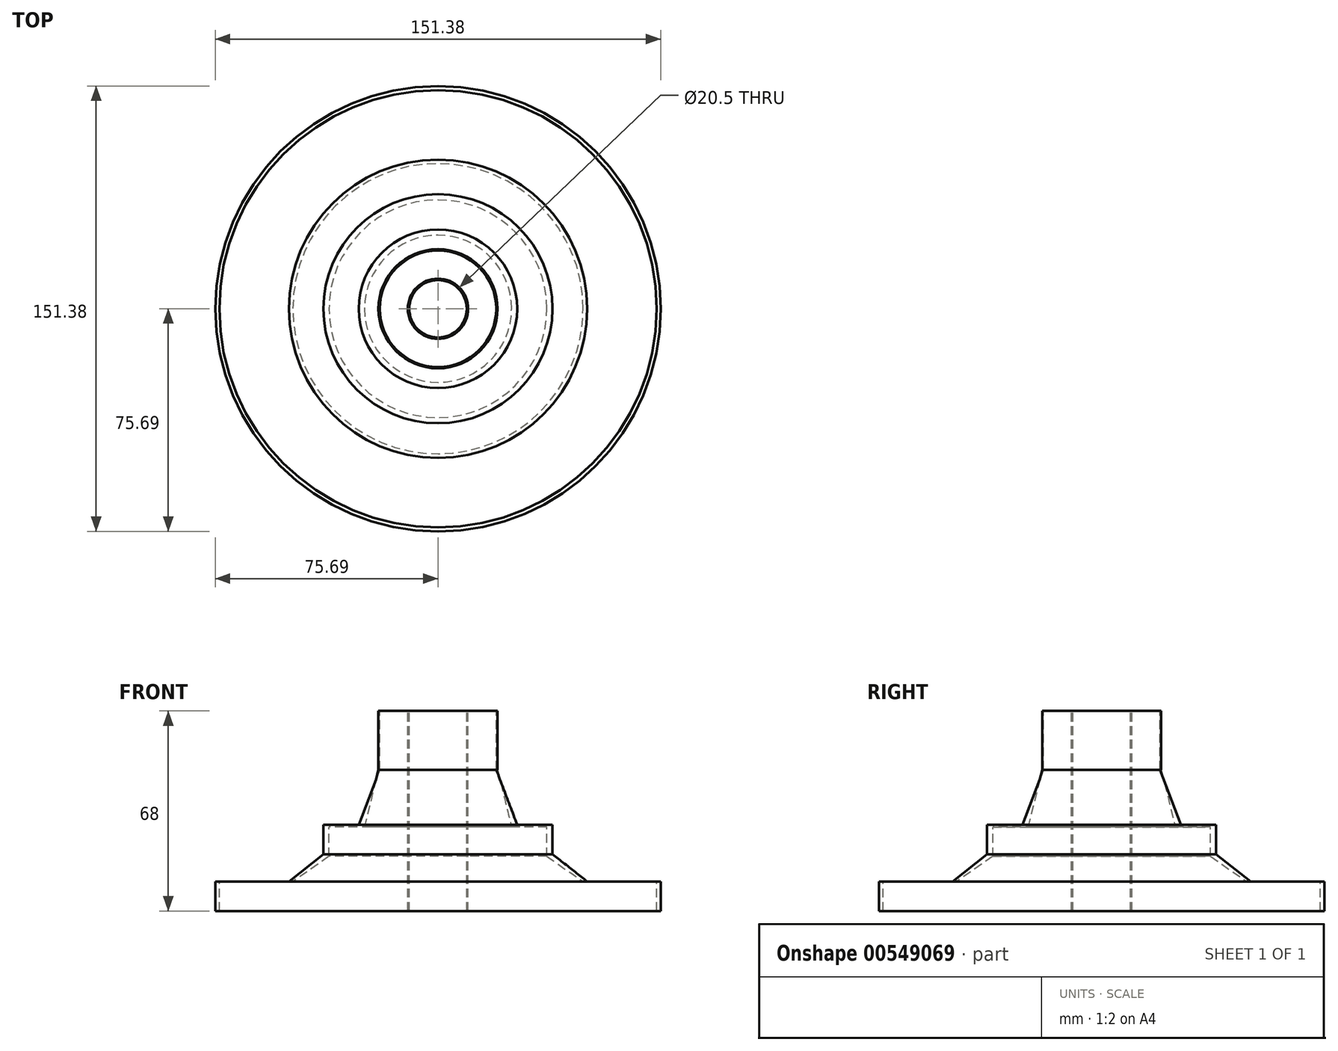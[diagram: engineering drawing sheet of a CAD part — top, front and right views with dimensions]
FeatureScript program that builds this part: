
annotation { "Feature Type Name" : "Feature", "Feature Type Description" : "" }
export const myFeature = defineFeature(function(context is Context, id is Id, definition is map)
    precondition{}
    {
        {
            var Q0;
            Q0=qCreatedBy(makeId("Front.planeOp"),FACE);
            var sketch = newSketch(context, id + "F0", { "sketchPlane" : qUnion([Q0])});
            skLineSegment(sketch, "E0", {"start": v(0, 68) * mm, "end": v(10, 68) * mm, "construction": true});
            skLineSegment(sketch, "E1", {"start": v(10, 68) * mm, "end": v(-10, 68) * mm, "construction": true});
            skLineSegment(sketch, "E2", {"start": v(-10, 68) * mm, "end": v(-10, 0) * mm, "construction": true});
            skLineSegment(sketch, "E3", {"start": v(-10, 0) * mm, "end": v(10, 0) * mm, "construction": true});
            skLineSegment(sketch, "E4", {"start": v(10, 0) * mm, "end": v(10, 68) * mm, "construction": true});
            skLineSegment(sketch, "E5", {"start": v(10, 68) * mm, "end": v(20, 68) * mm, "construction": true});
            skLineSegment(sketch, "E6", {"start": v(20, 68) * mm, "end": v(-20, 68) * mm, "construction": true});
            skLineSegment(sketch, "E7", {"start": v(-20, 68) * mm, "end": v(-20, 48) * mm, "construction": true});
            skLineSegment(sketch, "E8", {"start": v(20, 68) * mm, "end": v(20, 48) * mm, "construction": true});
            skLineSegment(sketch, "E9", {"start": v(0, 68) * mm, "end": v(0, 27.84) * mm, "construction": true});
            skLineSegment(sketch, "E10", {"start": v(0, 27.84) * mm, "end": v(-37.5, 27.84) * mm, "construction": true});
            skLineSegment(sketch, "E11", {"start": v(0, 27.84) * mm, "end": v(37.5, 27.84) * mm, "construction": true});
            skLineSegment(sketch, "E12", {"start": v(0, 68) * mm, "end": v(0, 18) * mm, "construction": true});
            skLineSegment(sketch, "E13", {"start": v(0, 68) * mm, "end": v(0, 10) * mm, "construction": true});
            skPoint(sketch, "E13.endSnap0", {"position": v(0, 43) * mm});
            skLineSegment(sketch, "E14", {"start": v(0, 10) * mm, "end": v(50, 10) * mm, "construction": true});
            skLineSegment(sketch, "E15", {"start": v(50, 10) * mm, "end": v(-50, 10) * mm, "construction": true});
            skLineSegment(sketch, "E16", {"start": v(0, 27.84) * mm, "end": v(-25, 27.84) * mm, "construction": true});
            skLineSegment(sketch, "E17", {"start": v(0, 27.84) * mm, "end": v(25, 27.84) * mm, "construction": true});
            skSolve(sketch);
        }
        {
            var Q0;
            Q0=qCreatedBy(makeId("Front.planeOp"),FACE);
            var sketch = newSketch(context, id + "F1", { "sketchPlane" : qUnion([Q0])});
            skLineSegment(sketch, "E18", {"start": v(-74.31, 0) * mm, "end": v(75.69, 0) * mm});
            skLineSegment(sketch, "E19", {"start": v(75.69, 0) * mm, "end": v(75.69, 10) * mm});
            skLineSegment(sketch, "E20", {"start": v(75.69, 10) * mm, "end": v(50.69, 10) * mm});
            skLineSegment(sketch, "E21", {"start": v(-74.31, 0) * mm, "end": v(-74.31, 10) * mm});
            skLineSegment(sketch, "E22", {"start": v(-74.31, 10) * mm, "end": v(-49.31, 10) * mm});
            skLineSegment(sketch, "E23", {"start": v(-10.25, 68) * mm, "end": v(-20.25, 68) * mm});
            skLineSegment(sketch, "E24", {"start": v(-20.25, 68) * mm, "end": v(-20.25, 48) * mm});
            skLineSegment(sketch, "E25", {"start": v(9.8, 68) * mm, "end": v(19.8, 68) * mm});
            skLineSegment(sketch, "E26", {"start": v(19.8, 68) * mm, "end": v(19.8, 48) * mm});
            skLineSegment(sketch, "E27", {"start": v(-10.25, 68) * mm, "end": v(-10.25, 0) * mm});
            skLineSegment(sketch, "E28", {"start": v(-10.25, 0) * mm, "end": v(9.75, 0) * mm});
            skLineSegment(sketch, "E29", {"start": v(9.75, 0) * mm, "end": v(9.8, 68) * mm});
            skLineSegment(sketch, "E30", {"start": v(38.93, 29.31) * mm, "end": v(38.93, 19.31) * mm});
            skLineSegment(sketch, "E31", {"start": v(38.93, 19.31) * mm, "end": v(50.69, 10) * mm});
            skLineSegment(sketch, "E32", {"start": v(-37, 28.57) * mm, "end": v(-37, 18.57) * mm});
            skLineSegment(sketch, "E33", {"start": v(-37, 18.57) * mm, "end": v(-49.31, 10) * mm});
            skLineSegment(sketch, "E34", {"start": v(-37, 28.57) * mm, "end": v(-25, 28.57) * mm});
            skLineSegment(sketch, "E35", {"start": v(38.93, 29.31) * mm, "end": v(26.93, 29.31) * mm});
            skLineSegment(sketch, "E36", {"start": v(-25, 28.57) * mm, "end": v(-20.25, 48) * mm});
            skLineSegment(sketch, "E37", {"start": v(19.8, 48) * mm, "end": v(26.93, 29.31) * mm});
            skSolve(sketch);
        }
        {
            var Q0;
            Q0 = qSketchRegion(id + "F1", true);
            var Q1;
            Q1=sQuery(id+"F0.wireOp",EDGE,"E13");
            revolve(context, id + "F2", {"entities" : qUnion([Q0]), "axis" : qUnion([Q1]), "revolveType" : RevolveType.FULL});
        }
    });
